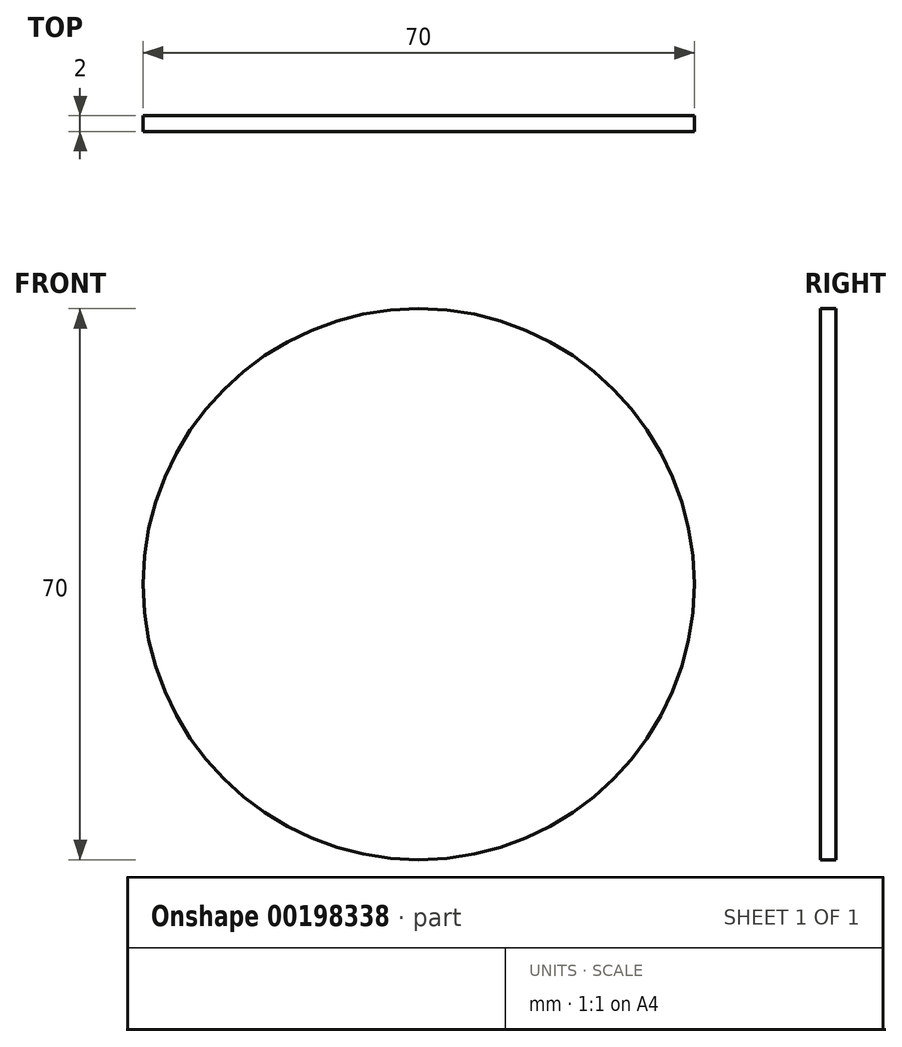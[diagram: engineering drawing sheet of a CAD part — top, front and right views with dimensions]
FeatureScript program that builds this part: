
annotation { "Feature Type Name" : "Feature", "Feature Type Description" : "" }
export const myFeature = defineFeature(function(context is Context, id is Id, definition is map)
    precondition{}
    {
        {
            var Q0;
            Q0=qCreatedBy(makeId("Front.planeOp"),FACE);
            cPlane(context, id + "F0", {"entities" : qUnion([Q0]), "cplaneType" : CPlaneType.OFFSET, "offset" : 60 * mm, "width" : 150 * mm, "height" : 150 * mm});
        }
        {
            var Q0;
            Q0=qCreatedBy(makeId("Front.planeOp"),FACE);
            var sketch = newSketch(context, id + "F1", { "sketchPlane" : qUnion([Q0])});
            skCircle(sketch, "E0", {"center": v(0, 0) * mm, "radius": 35 * mm});
            skCircle(sketch, "E1", {"center": v(0, 0) * mm, "radius": 26 * mm});
            skLineSegment(sketch, "E2", {"start": v(-25.98, -1) * mm, "end": v(25.98, -1) * mm});
            skSolve(sketch);
        }
        {
            assignVariable(context, id + "F2", {"name" : "THICKNESS", "anyValue" : 2});
        }
        {
            var Q0;
            Q0=qCreatedBy(id+"F0.planeOp",FACE);
            var sketch = newSketch(context, id + "F3", { "sketchPlane" : qUnion([Q0])});
            skCircle(sketch, "E3.0", {"center": v(0, 0) * mm, "radius": 35 * mm});
            skSolve(sketch);
        }
        {
            var Q0;
            Q0=qSketchRegion(id+"F3",true);
            extrude(context, id + "F4", {"entities" : qUnion([Q0]), "depth" : (getVariable(context, 'THICKNESS')) * mm});
        }
    });
